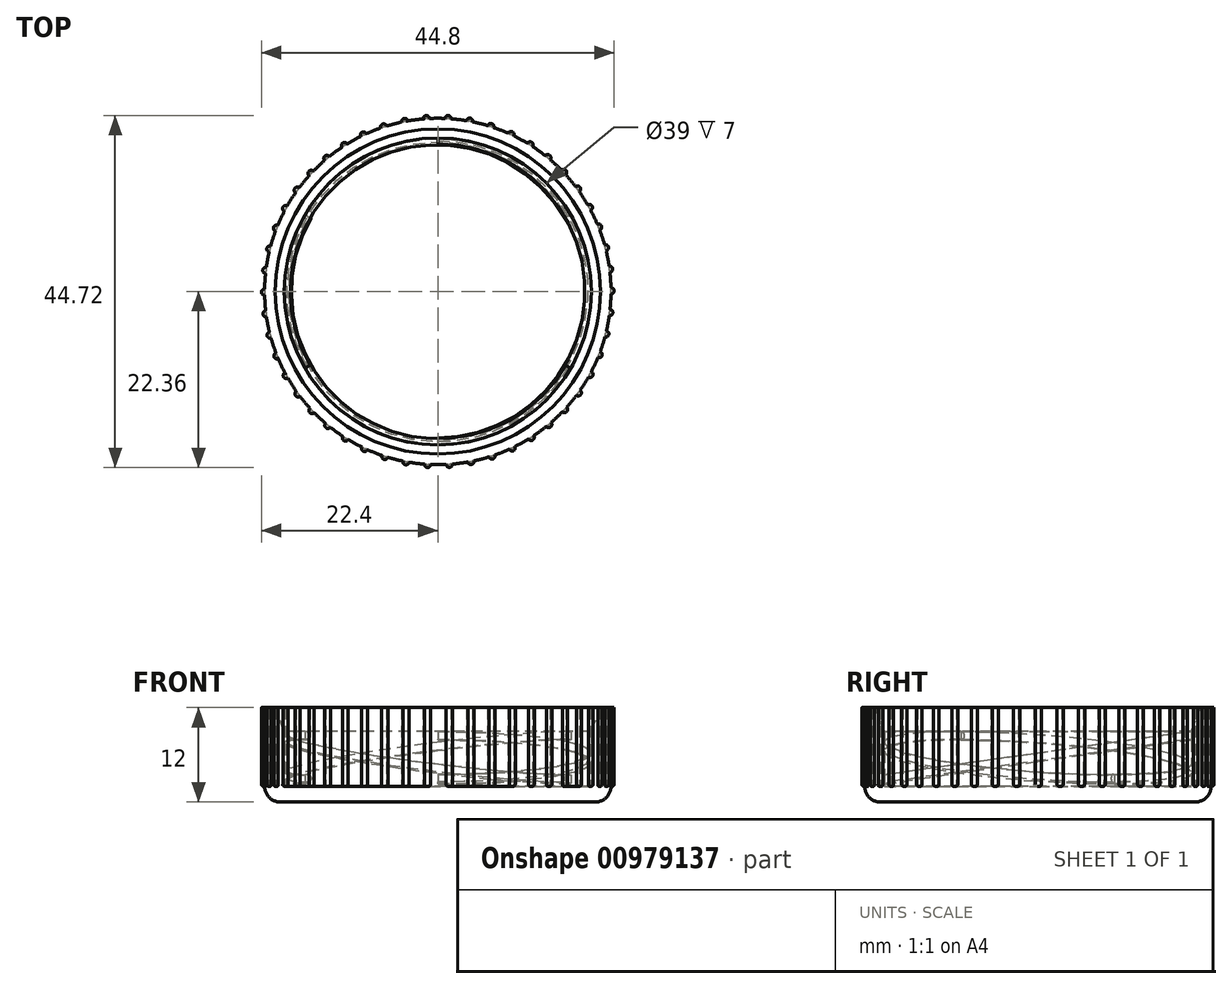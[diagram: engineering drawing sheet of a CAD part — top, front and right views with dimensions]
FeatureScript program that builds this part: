
annotation { "Feature Type Name" : "Feature", "Feature Type Description" : "" }
export const myFeature = defineFeature(function(context is Context, id is Id, definition is map)
    precondition{}
    {
        {
            var Q0;
            Q0=qCreatedBy(makeId("Top.planeOp"),FACE);
            var sketch = newSketch(context, id + "F0", { "sketchPlane" : qUnion([Q0])});
            skCircle(sketch, "E0", {"center": v(0, 0) * mm, "radius": 19.5 * mm});
            skCircle(sketch, "E1", {"center": v(0, 0) * mm, "radius": 22 * mm});
            skArc(sketch, "E2", {"start": v(22, -0.32) * mm, "mid": v(22.4, 0.08) * mm, "end": v(22, 0.48) * mm});
            skSolve(sketch);
        }
        {
            var Q0;
            Q0=qCreatedBy(makeId("Right.planeOp"),FACE);
            var sketch = newSketch(context, id + "F1", { "sketchPlane" : qUnion([Q0])});
            skLineSegment(sketch, "E3.bottom", {"start": v(-19.8, 7) * mm, "end": v(19.8, 7) * mm, "construction": true});
            skLineSegment(sketch, "E3.top", {"start": v(-19.8, 0) * mm, "end": v(19.8, 0) * mm, "construction": true});
            skLineSegment(sketch, "E3.left", {"start": v(-19.8, 7) * mm, "end": v(-19.8, 0) * mm, "construction": true});
            skLineSegment(sketch, "E3.right", {"start": v(19.8, 7) * mm, "end": v(19.8, 0) * mm, "construction": true});
            skPoint(sketch, "E4", {"position": v(0, 0) * mm});
            skLineSegment(sketch, "E5", {"start": v(-19.8, 1.4) * mm, "end": v(19.8, 7) * mm});
            skLineSegment(sketch, "E6", {"start": v(19.8, 7) * mm, "end": v(19.8, 5.83) * mm});
            skLineSegment(sketch, "E7", {"start": v(19.8, 5.83) * mm, "end": v(19.17, 5.94) * mm});
            skLineSegment(sketch, "E8", {"start": v(19.8, 7) * mm, "end": v(19.16, 6.9) * mm});
            skArc(sketch, "E9", {"start": v(19.16, 6.9) * mm, "mid": v(18.74, 6.42) * mm, "end": v(19.17, 5.94) * mm});
            skSolve(sketch);
        }
        {
            var Q0;
            Q0=makeQuery(id+"F0.imprint","IMPRINT",FACE,{"disambiguationData":[TD([[makeQuery(id+"F0.imprint","IMPRINT",EDGE,{"derivedFrom":sQuery(id+"F0.wireOp",EDGE,"E0")}),-1.0]])]});
            extrude(context, id + "F2", {"entities" : qUnion([Q0]), "depth" : 10 * mm, "offsetDistance" : 25 * mm});
        }
        {
            var Q0;
            Q0=sQuery(id+"F1.wireOp",EDGE,"E5");
            extrude(context, id + "F3", {"bodyType" : ToolBodyType.SURFACE, "flatOperationType" : FlatOperationType.REMOVE, "surfaceEntities" : qUnion([Q0]), "endBound" : BoundingType.UP_TO_NEXT, "depth" : 25 * mm, "offsetDistance" : 25 * mm, "domain" : OperationDomain.MODEL});
        }
        {
            var Q0;
            Q0=makeQuery(id+"F1.imprint","IMPRINT",FACE,{"disambiguationData":[TD([[makeQuery(id+"F1.imprint","IMPRINT",EDGE,{"derivedFrom":sQuery(id+"F1.wireOp",EDGE,"E6")}),-1.0]])]});
            var Q1;
            Q1=makeQuery(id+"F3.opExtrude","CAP_EDGE",EDGE,{"disambiguationData":[OSD([sQuery(id+"F1.wireOp",EDGE,"E5")])],"isStart":false});
            sweep(context, id + "F4", {"profiles" : qUnion([Q0]), "path" : qUnion([Q1])});
        }
        {
            var Q0;
            Q0=makeQuery(id+"F4.opSweep","SWEPT_BODY",BODY,{"disambiguationData":[OSD([sQuery(id+"F1.wireOp",EDGE,"E5"),sQuery(id+"F1.wireOp",EDGE,"E6"),sQuery(id+"F1.wireOp",EDGE,"E7"),sQuery(id+"F1.wireOp",EDGE,"E8"),sQuery(id+"F1.wireOp",EDGE,"E9")])]});
            var Q1;
            Q1=makeQuery(id+"F2.opExtrude","CAP_EDGE",EDGE,{"disambiguationData":[OSD([sQuery(id+"F0.wireOp",EDGE,"E0")])],"isStart":false});
            circularPattern(context, id + "F5", {"operationType" : NewBodyOperationType.ADD, "entities" : qUnion([Q0]), "axis" : qUnion([Q1]), "angle" : 360 * degree, "instanceCount" : 3, "equalSpace" : true});
        }
        {
            var Q0;
            Q0=makeQuery(id+"F2.opExtrude","CAP_EDGE",EDGE,{"disambiguationData":[OSD([sQuery(id+"F0.wireOp",EDGE,"E0")])],"isStart":false});
            chamfer(context, id + "F6", {"entities" : qUnion([Q0]), "chamferType" : ChamferType.OFFSET_ANGLE, "width" : 3 * mm, "oppositeDirection" : false, "angle" : 21 * degree, "tangentPropagation" : true});
        }
        {
            var Q0;
            Q0=makeQuery(id+"F2.opExtrude","CAP_FACE",FACE,{"disambiguationData":[OSD([sQuery(id+"F0.wireOp",EDGE,"E0"),sQuery(id+"F0.wireOp",EDGE,"E1")])],"isStart":true});
            var sketch = newSketch(context, id + "F7", { "sketchPlane" : qUnion([Q0])});
            skCircle(sketch, "E10", {"center": v(0, 0) * mm, "radius": 22 * mm});
            skSolve(sketch);
        }
        {
            var Q0;
            Q0 = qSketchRegion(id + "F7", true);
            extrude(context, id + "F8", {"entities" : qUnion([Q0]), "operationType" : NewBodyOperationType.ADD, "depth" : 2 * mm, "offsetDistance" : 25 * mm});
        }
        {
            var Q0;
            Q0=makeQuery(id+"F8.opExtrude","CAP_EDGE",EDGE,{"disambiguationData":[OSD([sQuery(id+"F7.wireOp",EDGE,"E10")])],"isStart":false});
            fillet(context, id + "F9", {"entities" : qUnion([Q0]), "tangentPropagation" : true, "radius" : 2 * mm, "defaultsChanged" : true, "vertexSettings" : [], "allowEdgeOverflow" : false});
        }
        {
            var Q0;
            {var subQ0=sQuery(id+"F0.wireOp",EDGE,"E2");Q0=makeQuery(id+"F0.imprint","IMPRINT",FACE,{"disambiguationData":[TD([[makeQuery(id+"F0.imprint","IMPRINT",EDGE,{"derivedFrom":subQ0}),1.0]])]});}
            var Q1;
            Q1=makeQuery(id+"F2.opExtrude","CAP_FACE",FACE,{"disambiguationData":[OSD([sQuery(id+"F0.wireOp",EDGE,"E0"),sQuery(id+"F0.wireOp",EDGE,"E1")])],"isStart":false});
            extrude(context, id + "F10", {"entities" : qUnion([Q0]), "endBound" : BoundingType.UP_TO_SURFACE, "depth" : 25 * mm, "endBoundEntityFace" : qUnion([Q1]), "offsetDistance" : 25 * mm});
        }
        {
            var Q0;
            Q0=makeQuery(id+"F10.opExtrude","CAP_EDGE",EDGE,{"disambiguationData":[OSD([sQuery(id+"F0.wireOp",EDGE,"E2")])],"isStart":true});
            fillet(context, id + "F11", {"entities" : qUnion([Q0]), "tangentPropagation" : true, "radius" : 0.25 * mm, "defaultsChanged" : true, "vertexSettings" : [], "allowEdgeOverflow" : false});
        }
        {
            var Q0;
            Q0=makeQuery(id+"F10.opExtrude","SWEPT_BODY",BODY,{"disambiguationData":[OSD([sQuery(id+"F0.wireOp",EDGE,"E1"),sQuery(id+"F0.wireOp",EDGE,"E2")])]});
            var Q1;
            Q1=makeQuery(id+"F2.opExtrude","CAP_EDGE",EDGE,{"disambiguationData":[OSD([sQuery(id+"F0.wireOp",EDGE,"E1")])],"isStart":false});
            circularPattern(context, id + "F12", {"operationType" : NewBodyOperationType.ADD, "entities" : qUnion([Q0]), "axis" : qUnion([Q1]), "angle" : 360 * degree, "instanceCount" : 50, "equalSpace" : true, "isCentered" : true});
        }
        {
            var Q0;
            Q0=makeQuery(id+"F3.opExtrude","SWEPT_BODY",BODY,{"disambiguationData":[OSD([sQuery(id+"F1.wireOp",EDGE,"E5")])]});
            deleteBodies(context, id + "F13", {"entities" : qUnion([Q0])});
        }
    });
